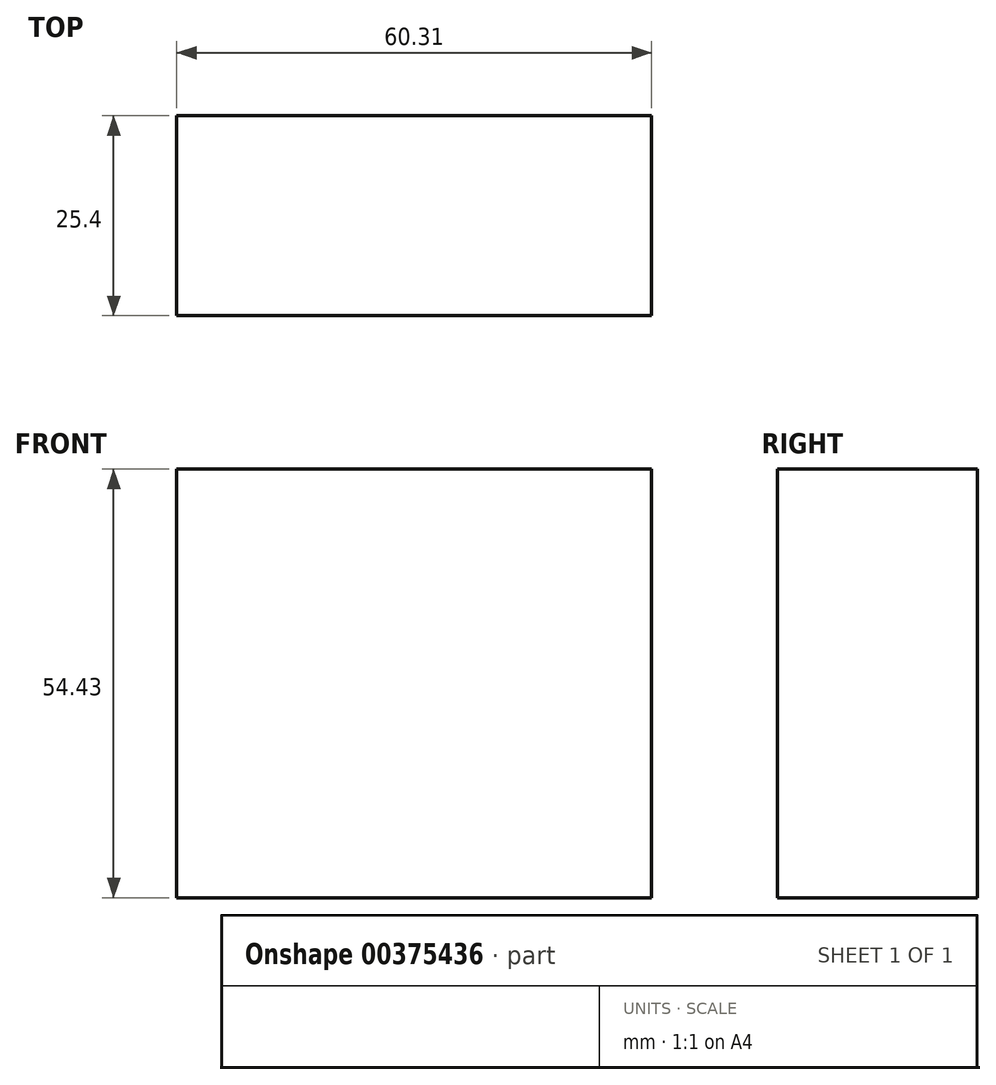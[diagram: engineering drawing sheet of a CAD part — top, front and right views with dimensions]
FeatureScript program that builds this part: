
annotation { "Feature Type Name" : "Feature", "Feature Type Description" : "" }
export const myFeature = defineFeature(function(context is Context, id is Id, definition is map)
    precondition{}
    {
        {
            var Q0;
            Q0=qCreatedBy(makeId("Front.planeOp"),FACE);
            var sketch = newSketch(context, id + "F0", { "sketchPlane" : qUnion([Q0])});
            skLineSegment(sketch, "E0.bottom", {"start": v(0, 0) * mm, "end": v(60.3, 0) * mm});
            skLineSegment(sketch, "E0.top", {"start": v(0, 54.43) * mm, "end": v(60.3, 54.43) * mm});
            skLineSegment(sketch, "E0.left", {"start": v(0, 0) * mm, "end": v(0, 54.43) * mm});
            skLineSegment(sketch, "E0.right", {"start": v(60.3, 0) * mm, "end": v(60.3, 54.43) * mm});
            skSolve(sketch);
        }
        {
            var Q0;
            Q0 = qSketchRegion(id + "F0", true);
            extrude(context, id + "F1", {"entities" : qUnion([Q0]), "depth" : 25.4 * mm});
        }
    });
